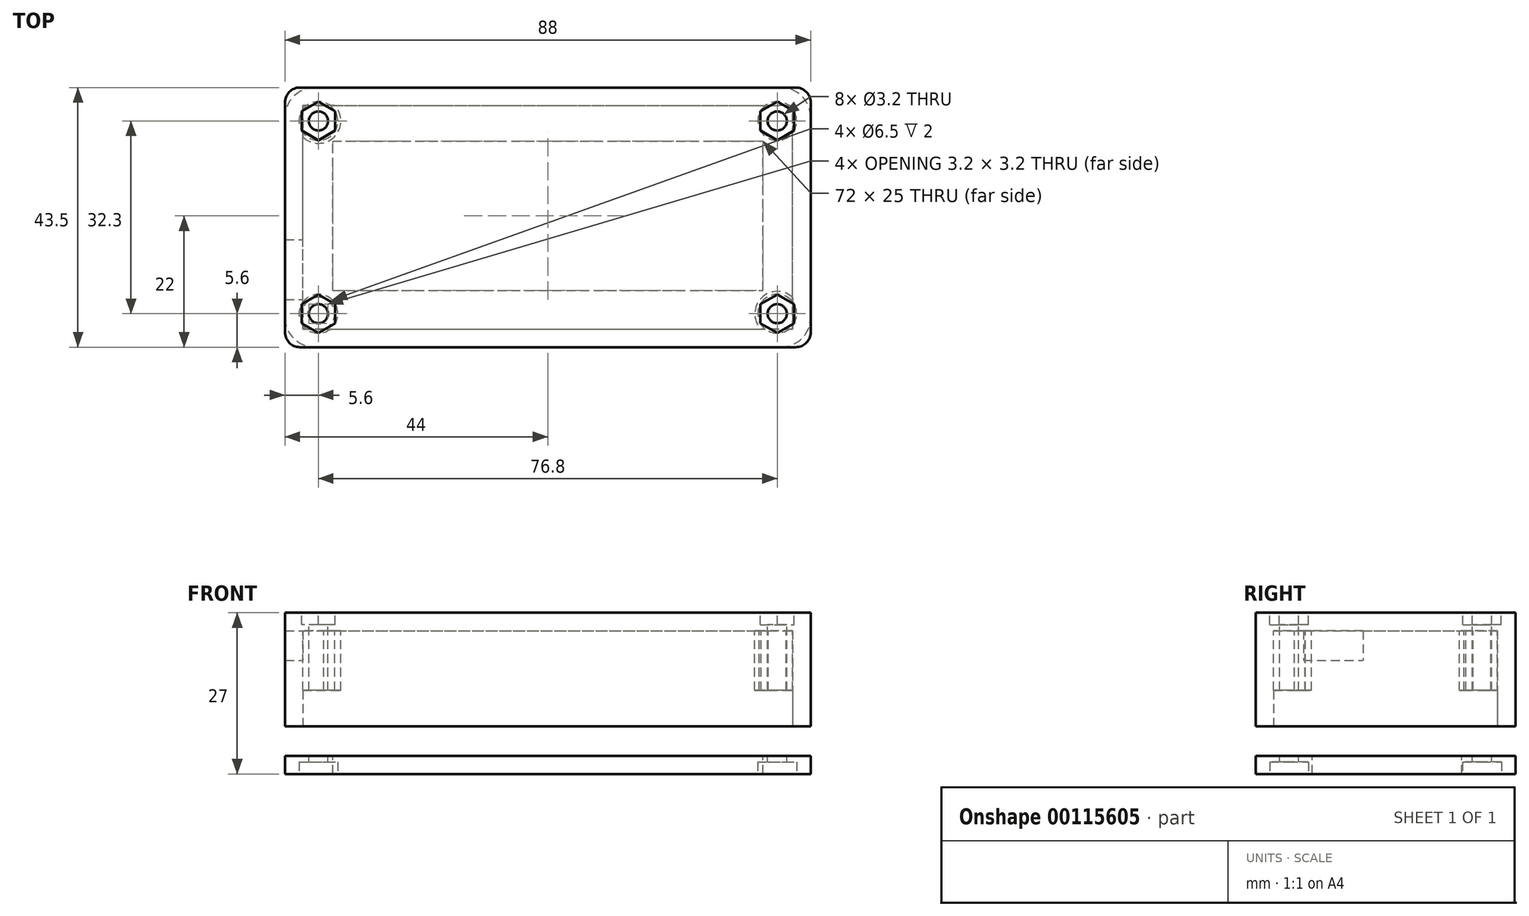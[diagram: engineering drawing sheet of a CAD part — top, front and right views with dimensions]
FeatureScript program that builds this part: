
annotation { "Feature Type Name" : "Feature", "Feature Type Description" : "" }
export const myFeature = defineFeature(function(context is Context, id is Id, definition is map)
    precondition{}
    {
        {
            var Q0;
            Q0=qCreatedBy(makeId("Top.planeOp"),FACE);
            var sketch = newSketch(context, id + "F0", { "sketchPlane" : qUnion([Q0])});
            skLineSegment(sketch, "E0.bottom", {"start": v(0, 0) * mm, "end": v(82, 0) * mm});
            skLineSegment(sketch, "E0.top", {"start": v(0, 37.5) * mm, "end": v(82, 37.5) * mm});
            skLineSegment(sketch, "E0.left", {"start": v(0, 0) * mm, "end": v(0, 37.5) * mm});
            skLineSegment(sketch, "E0.right", {"start": v(82, 0) * mm, "end": v(82, 37.5) * mm});
            skLineSegment(sketch, "E1.0", {"start": v(-3, 40.5) * mm, "end": v(85, 40.5) * mm});
            skLineSegment(sketch, "E1.1", {"start": v(-3, -3) * mm, "end": v(-3, 40.5) * mm});
            skLineSegment(sketch, "E1.2", {"start": v(-3, -3) * mm, "end": v(85, -3) * mm});
            skLineSegment(sketch, "E1.3", {"start": v(85, -3) * mm, "end": v(85, 40.5) * mm});
            skSolve(sketch);
        }
        {
            var Q0;
            Q0=makeQuery(id+"F0.imprint","IMPRINT",FACE,{"disambiguationData":[TD([[makeQuery(id+"F0.imprint","IMPRINT",EDGE,{"derivedFrom":sQuery(id+"F0.wireOp",EDGE,"E0.bottom")}),-1.0]])]});
            extrude(context, id + "F1", {"entities" : qUnion([Q0]), "depth" : 16 * mm});
        }
        {
            var Q0;
            Q0=makeQuery(id+"F1.opExtrude","CAP_FACE",FACE,{"disambiguationData":[OSD([sQuery(id+"F0.wireOp",EDGE,"E0.bottom"),sQuery(id+"F0.wireOp",EDGE,"E0.top"),sQuery(id+"F0.wireOp",EDGE,"E0.left"),sQuery(id+"F0.wireOp",EDGE,"E0.right"),sQuery(id+"F0.wireOp",EDGE,"E1.0"),sQuery(id+"F0.wireOp",EDGE,"E1.1"),sQuery(id+"F0.wireOp",EDGE,"E1.2"),sQuery(id+"F0.wireOp",EDGE,"E1.3")])],"isStart":false});
            var sketch = newSketch(context, id + "F2", { "sketchPlane" : qUnion([Q0])});
            skLineSegment(sketch, "E2.bottom", {"start": v(-3, 40.5) * mm, "end": v(85, 40.5) * mm});
            skLineSegment(sketch, "E2.top", {"start": v(-3, -3) * mm, "end": v(85, -3) * mm});
            skLineSegment(sketch, "E2.left", {"start": v(-3, 40.5) * mm, "end": v(-3, -3) * mm});
            skLineSegment(sketch, "E2.right", {"start": v(85, 40.5) * mm, "end": v(85, -3) * mm});
            skSolve(sketch);
        }
        {
            var Q0;
            Q0 = qSketchRegion(id + "F2", true);
            extrude(context, id + "F3", {"entities" : qUnion([Q0]), "operationType" : NewBodyOperationType.ADD, "depth" : 3 * mm});
        }
        {
            var Q0;
            Q0=makeQuery(id+"F3.opExtrude","CAP_FACE",FACE,{"disambiguationData":[OSD([sQuery(id+"F2.wireOp",EDGE,"E2.bottom"),sQuery(id+"F2.wireOp",EDGE,"E2.top"),sQuery(id+"F2.wireOp",EDGE,"E2.left"),sQuery(id+"F2.wireOp",EDGE,"E2.right")])],"isStart":true});
            var sketch = newSketch(context, id + "F4", { "sketchPlane" : qUnion([Q0])});
            skCircle(sketch, "E3", {"center": v(79.4, -34.9) * mm, "radius": 1.6 * mm});
            skCircle(sketch, "E4", {"center": v(79.4, -2.6) * mm, "radius": 1.6 * mm});
            skCircle(sketch, "E5", {"center": v(2.6, -2.6) * mm, "radius": 1.6 * mm});
            skCircle(sketch, "E6", {"center": v(2.6, -34.9) * mm, "radius": 1.6 * mm});
            skArc(sketch, "E7", {"start": v(-0.15, -2.66) * mm, "mid": v(4.5, -4.6) * mm, "end": v(2.8, 0.14) * mm});
            skCircle(sketch, "E8", {"center": v(79.4, -2.6) * mm, "radius": 3.75 * mm});
            skCircle(sketch, "E9", {"center": v(79.4, -34.9) * mm, "radius": 3 * mm});
            skCircle(sketch, "E10", {"center": v(2.6, -34.9) * mm, "radius": 3.75 * mm});
            skLineSegment(sketch, "E11", {"start": v(2.8, 0.14) * mm, "end": v(-0.67, 0.43) * mm});
            skLineSegment(sketch, "E12", {"start": v(-0.67, 0.43) * mm, "end": v(-0.15, -2.66) * mm});
            skSolve(sketch);
        }
        {
            var Q0;
            Q0 = qSketchRegion(id + "F4", true);
            extrude(context, id + "F5", {"entities" : qUnion([Q0]), "operationType" : NewBodyOperationType.ADD, "depth" : 10 * mm});
        }
        {
            var Q0;
            Q0=makeQuery(id+"F1.opExtrude","SWEPT_FACE",FACE,{"disambiguationData":[OSD([sQuery(id+"F0.wireOp",EDGE,"E0.left")])]});
            var sketch = newSketch(context, id + "F6", { "sketchPlane" : qUnion([Q0])});
            skLineSegment(sketch, "E13.bottom", {"start": v(5, 16) * mm, "end": v(15, 16) * mm});
            skLineSegment(sketch, "E13.top", {"start": v(5, 11) * mm, "end": v(15, 11) * mm});
            skLineSegment(sketch, "E13.left", {"start": v(5, 16) * mm, "end": v(5, 11) * mm});
            skLineSegment(sketch, "E13.right", {"start": v(15, 16) * mm, "end": v(15, 11) * mm});
            skSolve(sketch);
        }
        {
            var Q0;
            Q0 = qSketchRegion(id + "F6", true);
            extrude(context, id + "F7", {"entities" : qUnion([Q0]), "operationType" : NewBodyOperationType.REMOVE, "oppositeDirection" : true, "depth" : 25 * mm});
        }
        {
            var Q0;
            Q0=makeQuery(id+"F5.opExtrude","CAP_FACE",FACE,{"disambiguationData":[OSD([sQuery(id+"F4.wireOp",EDGE,"E5"),sQuery(id+"F4.wireOp",EDGE,"E7"),sQuery(id+"F4.wireOp",EDGE,"E11"),sQuery(id+"F4.wireOp",EDGE,"E12")])],"isStart":false});
            var sketch = newSketch(context, id + "F8", { "sketchPlane" : qUnion([Q0])});
            skCircle(sketch, "E14.0", {"center": v(2.6, -2.6) * mm, "radius": 1.6 * mm});
            skCircle(sketch, "E15.0", {"center": v(2.6, -34.9) * mm, "radius": 1.6 * mm});
            skCircle(sketch, "E16.0", {"center": v(79.4, -34.9) * mm, "radius": 1.6 * mm});
            skCircle(sketch, "E17.0", {"center": v(79.4, -2.6) * mm, "radius": 1.6 * mm});
            skSolve(sketch);
        }
        {
            var Q0;
            Q0 = qSketchRegion(id + "F8", true);
            extrude(context, id + "F9", {"entities" : qUnion([Q0]), "operationType" : NewBodyOperationType.REMOVE, "oppositeDirection" : true, "depth" : 25 * mm});
        }
        {
            var Q0;
            Q0=makeQuery(id+"F3.opExtrude","CAP_FACE",FACE,{"disambiguationData":[OSD([sQuery(id+"F2.wireOp",EDGE,"E2.bottom"),sQuery(id+"F2.wireOp",EDGE,"E2.top"),sQuery(id+"F2.wireOp",EDGE,"E2.left"),sQuery(id+"F2.wireOp",EDGE,"E2.right")])],"isStart":false});
            var sketch = newSketch(context, id + "F10", { "sketchPlane" : qUnion([Q0])});
            skCircle(sketch, "E18.cCircle", {"center": v(2.6, 2.6) * mm, "radius": 2.8 * mm, "construction": true});
            skLineSegment(sketch, "E18.0", {"start": v(-0.2, 0.98) * mm, "end": v(-0.2, 4.22) * mm});
            skLineSegment(sketch, "E18.1", {"start": v(-0.2, 4.22) * mm, "end": v(2.6, 5.83) * mm});
            skLineSegment(sketch, "E18.2", {"start": v(2.6, 5.83) * mm, "end": v(5.4, 4.22) * mm});
            skLineSegment(sketch, "E18.3", {"start": v(5.4, 4.22) * mm, "end": v(5.4, 0.98) * mm});
            skLineSegment(sketch, "E18.4", {"start": v(5.4, 0.98) * mm, "end": v(2.6, -0.63) * mm});
            skLineSegment(sketch, "E18.5", {"start": v(2.6, -0.63) * mm, "end": v(-0.2, 0.98) * mm});
            skPoint(sketch, "E18.0.midPoint", {"position": v(-0.2, 2.6) * mm});
            skCircle(sketch, "E19.cCircle", {"center": v(2.6, 34.9) * mm, "radius": 2.8 * mm, "construction": true});
            skLineSegment(sketch, "E19.0", {"start": v(-0.2, 33.28) * mm, "end": v(-0.2, 36.52) * mm});
            skLineSegment(sketch, "E19.1", {"start": v(-0.2, 36.52) * mm, "end": v(2.6, 38.13) * mm});
            skLineSegment(sketch, "E19.2", {"start": v(2.6, 38.13) * mm, "end": v(5.4, 36.52) * mm});
            skLineSegment(sketch, "E19.3", {"start": v(5.4, 36.52) * mm, "end": v(5.4, 33.28) * mm});
            skLineSegment(sketch, "E19.4", {"start": v(5.4, 33.28) * mm, "end": v(2.6, 31.67) * mm});
            skLineSegment(sketch, "E19.5", {"start": v(2.6, 31.67) * mm, "end": v(-0.2, 33.28) * mm});
            skPoint(sketch, "E19.0.midPoint", {"position": v(-0.2, 34.9) * mm});
            skCircle(sketch, "E20.cCircle", {"center": v(79.4, 2.6) * mm, "radius": 2.8 * mm, "construction": true});
            skLineSegment(sketch, "E20.0", {"start": v(82.2, 4.22) * mm, "end": v(82.2, 0.98) * mm});
            skLineSegment(sketch, "E20.1", {"start": v(82.2, 0.98) * mm, "end": v(79.4, -0.63) * mm});
            skLineSegment(sketch, "E20.2", {"start": v(79.4, -0.63) * mm, "end": v(76.6, 0.98) * mm});
            skLineSegment(sketch, "E20.3", {"start": v(76.6, 0.98) * mm, "end": v(76.6, 4.22) * mm});
            skLineSegment(sketch, "E20.4", {"start": v(76.6, 4.22) * mm, "end": v(79.4, 5.83) * mm});
            skLineSegment(sketch, "E20.5", {"start": v(79.4, 5.83) * mm, "end": v(82.2, 4.22) * mm});
            skPoint(sketch, "E20.0.midPoint", {"position": v(82.2, 2.6) * mm});
            skCircle(sketch, "E21.cCircle", {"center": v(79.4, 34.9) * mm, "radius": 2.8 * mm, "construction": true});
            skLineSegment(sketch, "E21.0", {"start": v(82.2, 36.52) * mm, "end": v(82.2, 33.28) * mm});
            skLineSegment(sketch, "E21.1", {"start": v(82.2, 33.28) * mm, "end": v(79.4, 31.67) * mm});
            skLineSegment(sketch, "E21.2", {"start": v(79.4, 31.67) * mm, "end": v(76.6, 33.28) * mm});
            skLineSegment(sketch, "E21.3", {"start": v(76.6, 33.28) * mm, "end": v(76.6, 36.52) * mm});
            skLineSegment(sketch, "E21.4", {"start": v(76.6, 36.52) * mm, "end": v(79.4, 38.13) * mm});
            skLineSegment(sketch, "E21.5", {"start": v(79.4, 38.13) * mm, "end": v(82.2, 36.52) * mm});
            skPoint(sketch, "E21.0.midPoint", {"position": v(82.2, 34.9) * mm});
            skSolve(sketch);
        }
        {
            var Q0;
            Q0 = qSketchRegion(id + "F10", true);
            extrude(context, id + "F11", {"entities" : qUnion([Q0]), "operationType" : NewBodyOperationType.REMOVE, "oppositeDirection" : true, "depth" : 2 * mm});
        }
        {
            var Q0;
            Q0=makeQuery(id+"F3.boolean.opBoolean","MERGE",EDGE,{"derivedFrom":[makeQuery(id+"F1.opExtrude","SWEPT_EDGE",EDGE,{"disambiguationData":[OSD([sQuery(id+"F0.wireOp",EDGE,"E1.1"),sQuery(id+"F0.wireOp",EDGE,"E1.2")])]}),makeQuery(id+"F3.opExtrude","SWEPT_EDGE",EDGE,{"disambiguationData":[OSD([sQuery(id+"F2.wireOp",EDGE,"E2.top"),sQuery(id+"F2.wireOp",EDGE,"E2.left")])]})]});
            var Q1;
            Q1=makeQuery(id+"F3.boolean.opBoolean","MERGE",EDGE,{"derivedFrom":[makeQuery(id+"F1.opExtrude","SWEPT_EDGE",EDGE,{"disambiguationData":[OSD([sQuery(id+"F0.wireOp",EDGE,"E1.2"),sQuery(id+"F0.wireOp",EDGE,"E1.3")])]}),makeQuery(id+"F3.opExtrude","SWEPT_EDGE",EDGE,{"disambiguationData":[OSD([sQuery(id+"F2.wireOp",EDGE,"E2.top"),sQuery(id+"F2.wireOp",EDGE,"E2.right")])]})]});
            var Q2;
            Q2=makeQuery(id+"F3.boolean.opBoolean","MERGE",EDGE,{"derivedFrom":[makeQuery(id+"F1.opExtrude","SWEPT_EDGE",EDGE,{"disambiguationData":[OSD([sQuery(id+"F0.wireOp",EDGE,"E1.0"),sQuery(id+"F0.wireOp",EDGE,"E1.3")])]}),makeQuery(id+"F3.opExtrude","SWEPT_EDGE",EDGE,{"disambiguationData":[OSD([sQuery(id+"F2.wireOp",EDGE,"E2.bottom"),sQuery(id+"F2.wireOp",EDGE,"E2.right")])]})]});
            var Q3;
            Q3=makeQuery(id+"F3.boolean.opBoolean","MERGE",EDGE,{"derivedFrom":[makeQuery(id+"F1.opExtrude","SWEPT_EDGE",EDGE,{"disambiguationData":[OSD([sQuery(id+"F0.wireOp",EDGE,"E1.0"),sQuery(id+"F0.wireOp",EDGE,"E1.1")])]}),makeQuery(id+"F3.opExtrude","SWEPT_EDGE",EDGE,{"disambiguationData":[OSD([sQuery(id+"F2.wireOp",EDGE,"E2.bottom"),sQuery(id+"F2.wireOp",EDGE,"E2.left")])]})]});
            fillet(context, id + "F12", {"entities" : qUnion([Q0, Q1, Q2, Q3]), "radius" : 2.5 * mm, "tangentPropagation" : true, "allowEdgeOverflow" : false});
        }
        {
            var Q0;
            Q0=qCreatedBy(makeId("Top.planeOp"),FACE);
            cPlane(context, id + "F13", {"entities" : qUnion([Q0]), "cplaneType" : CPlaneType.OFFSET, "offset" : 5 * mm, "oppositeDirection" : true, "width" : 150 * mm, "height" : 150 * mm});
        }
        {
            var Q0;
            Q0=qCreatedBy(id+"F13.planeOp",FACE);
            var sketch = newSketch(context, id + "F14", { "sketchPlane" : qUnion([Q0])});
            skLineSegment(sketch, "E22.bottom", {"start": v(5, 6.5) * mm, "end": v(77, 6.5) * mm});
            skLineSegment(sketch, "E22.top", {"start": v(5, 31.5) * mm, "end": v(77, 31.5) * mm});
            skLineSegment(sketch, "E22.left", {"start": v(5, 6.5) * mm, "end": v(5, 31.5) * mm});
            skLineSegment(sketch, "E22.right", {"start": v(77, 6.5) * mm, "end": v(77, 31.5) * mm});
            skLineSegment(sketch, "E23", {"start": v(-3, 2) * mm, "end": v(-3, 35.5) * mm});
            skLineSegment(sketch, "E24", {"start": v(2, 40.5) * mm, "end": v(80, 40.5) * mm});
            skLineSegment(sketch, "E25", {"start": v(85, 35.5) * mm, "end": v(85, 2) * mm});
            skLineSegment(sketch, "E26", {"start": v(80, -3) * mm, "end": v(2, -3) * mm});
            skCircle(sketch, "E27", {"center": v(2.6, 2.6) * mm, "radius": 1.6 * mm});
            skCircle(sketch, "E28.0", {"center": v(2.6, 34.9) * mm, "radius": 1.6 * mm});
            skCircle(sketch, "E29.0", {"center": v(79.4, 34.9) * mm, "radius": 1.6 * mm});
            skCircle(sketch, "E30.0", {"center": v(79.4, 2.6) * mm, "radius": 1.6 * mm});
            skPoint(sketch, "E31.visualSharp", {"position": v(85, -3) * mm});
            skArc(sketch, "E31.filletArc", {"start": v(80, -3) * mm, "mid": v(83.54, -1.54) * mm, "end": v(85, 2) * mm});
            skPoint(sketch, "E32.visualSharp", {"position": v(85, 40.5) * mm});
            skArc(sketch, "E32.filletArc", {"start": v(85, 35.5) * mm, "mid": v(83.54, 39.04) * mm, "end": v(80, 40.5) * mm});
            skPoint(sketch, "E33.visualSharp", {"position": v(-3, 40.5) * mm});
            skArc(sketch, "E33.filletArc", {"start": v(2, 40.5) * mm, "mid": v(-1.54, 39.04) * mm, "end": v(-3, 35.5) * mm});
            skPoint(sketch, "E34.visualSharp", {"position": v(-3, -3) * mm});
            skArc(sketch, "E34.filletArc", {"start": v(-3, 2) * mm, "mid": v(-1.54, -1.54) * mm, "end": v(2, -3) * mm});
            skSolve(sketch);
        }
        {
            var Q0;
            Q0 = qSketchRegion(id + "F14", true);
            extrude(context, id + "F15", {"entities" : qUnion([Q0]), "oppositeDirection" : true, "depth" : 3 * mm});
        }
        {
            var Q0;
            Q0=makeQuery(id+"F15.opExtrude","CAP_FACE",FACE,{"disambiguationData":[OSD([sQuery(id+"F14.wireOp",EDGE,"E22.bottom"),sQuery(id+"F14.wireOp",EDGE,"E22.top"),sQuery(id+"F14.wireOp",EDGE,"E22.left"),sQuery(id+"F14.wireOp",EDGE,"E22.right"),sQuery(id+"F14.wireOp",EDGE,"E23"),sQuery(id+"F14.wireOp",EDGE,"E24"),sQuery(id+"F14.wireOp",EDGE,"E25"),sQuery(id+"F14.wireOp",EDGE,"E26"),sQuery(id+"F14.wireOp",EDGE,"E27"),sQuery(id+"F14.wireOp",EDGE,"E28.0"),sQuery(id+"F14.wireOp",EDGE,"E29.0"),sQuery(id+"F14.wireOp",EDGE,"E30.0"),sQuery(id+"F14.wireOp",EDGE,"E31.filletArc"),sQuery(id+"F14.wireOp",EDGE,"E32.filletArc"),sQuery(id+"F14.wireOp",EDGE,"E33.filletArc"),sQuery(id+"F14.wireOp",EDGE,"E34.filletArc")])],"isStart":false});
            var sketch = newSketch(context, id + "F16", { "sketchPlane" : qUnion([Q0])});
            skCircle(sketch, "E35", {"center": v(2.6, -2.6) * mm, "radius": 3.25 * mm});
            skCircle(sketch, "E36", {"center": v(79.4, -2.6) * mm, "radius": 3.25 * mm});
            skCircle(sketch, "E37", {"center": v(79.4, -34.9) * mm, "radius": 3.25 * mm});
            skCircle(sketch, "E38", {"center": v(2.6, -34.9) * mm, "radius": 3.25 * mm});
            skSolve(sketch);
        }
        {
            var Q0;
            Q0 = qSketchRegion(id + "F16", true);
            extrude(context, id + "F17", {"entities" : qUnion([Q0]), "operationType" : NewBodyOperationType.REMOVE, "oppositeDirection" : true, "depth" : 2 * mm});
        }
    });
